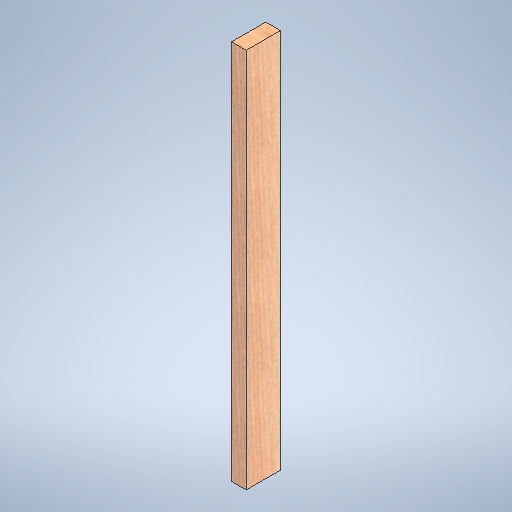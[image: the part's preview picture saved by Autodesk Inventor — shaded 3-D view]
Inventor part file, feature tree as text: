
AUTODESK INVENTOR PART (.ipt)
format: ipt  version: 2025.1 (Build 291241020, 241B)  size: 322,560 bytes
history: native  units: in
note: dims shown in document units (in); Inventor stores cm internally (conversion verified against a paired STEP export)
features: extrude x1, sketch x1
ambient origin geometry x8: Origin, YZ Plane, XZ Plane, XY Plane, X Axis, Y Axis, Z Axis, Center Point
bodies: Solid1 (feature_tree)
feature tree (2):
  extrude  "Extrusion1"  Depth=1.5in
  sketch  "Sketch1"  dims[d0=3.5in d1=1.5in d2=39.0in d3=0.0in]
